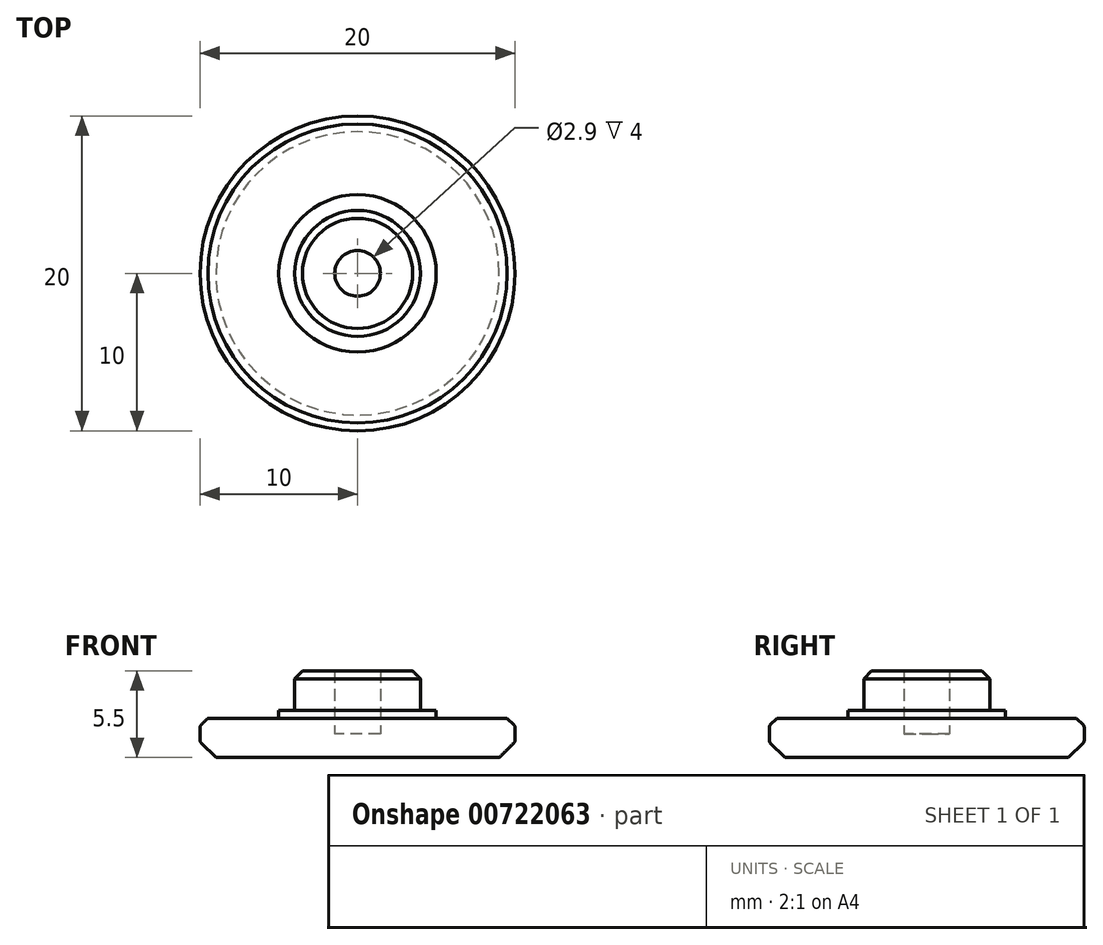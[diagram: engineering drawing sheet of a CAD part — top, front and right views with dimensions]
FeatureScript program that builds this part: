
annotation { "Feature Type Name" : "Feature", "Feature Type Description" : "" }
export const myFeature = defineFeature(function(context is Context, id is Id, definition is map)
    precondition{}
    {
        {
            var Q0;
            Q0=qCreatedBy(makeId("Top.planeOp"),FACE);
            var sketch = newSketch(context, id + "F0", { "sketchPlane" : qUnion([Q0])});
            skCircle(sketch, "E0", {"center": v(0, 0) * mm, "radius": 4 * mm});
            skSolve(sketch);
        }
        {
            var Q0;
            Q0=makeQuery(id+"F0.imprint","IMPRINT",FACE,{"disambiguationData":[TD([[makeQuery(id+"F0.imprint","IMPRINT",EDGE,{"derivedFrom":sQuery(id+"F0.wireOp",EDGE,"E0")}),1.0]])]});
            extrude(context, id + "F1", {"entities" : qUnion([Q0]), "depth" : 5.5 * mm, "offsetDistance" : 25 * mm});
        }
        {
            var Q0;
            Q0=qCreatedBy(makeId("Top.planeOp"),FACE);
            var sketch = newSketch(context, id + "F2", { "sketchPlane" : qUnion([Q0])});
            skCircle(sketch, "E1", {"center": v(0, 0) * mm, "radius": 5 * mm});
            skSolve(sketch);
        }
        {
            var Q0;
            Q0=makeQuery(id+"F2.imprint","IMPRINT",FACE,{"disambiguationData":[TD([[makeQuery(id+"F2.imprint","IMPRINT",EDGE,{"derivedFrom":sQuery(id+"F2.wireOp",EDGE,"E1")}),1.0]])]});
            extrude(context, id + "F3", {"entities" : qUnion([Q0]), "operationType" : NewBodyOperationType.ADD, "depth" : 3 * mm, "offsetDistance" : 25 * mm});
        }
        {
            var Q0;
            Q0=qCreatedBy(makeId("Top.planeOp"),FACE);
            var sketch = newSketch(context, id + "F4", { "sketchPlane" : qUnion([Q0])});
            skCircle(sketch, "E2", {"center": v(0, 0) * mm, "radius": 10 * mm});
            skSolve(sketch);
        }
        {
            var Q0;
            Q0=qSketchRegion(id+"F4",true);
            extrude(context, id + "F5", {"entities" : qUnion([Q0]), "operationType" : NewBodyOperationType.ADD, "depth" : 2.5 * mm, "offsetDistance" : 25 * mm});
        }
        {
            var Q0;
            Q0=makeQuery(id+"F5.opExtrude","CAP_EDGE",EDGE,{"disambiguationData":[OSD([sQuery(id+"F4.wireOp",EDGE,"E2")])],"isStart":true});
            chamfer(context, id + "F6", {"entities" : qUnion([Q0]), "width" : 1 * mm, "tangentPropagation" : true});
        }
        {
            var Q0;
            Q0=makeQuery(id+"F5.opExtrude","CAP_EDGE",EDGE,{"disambiguationData":[OSD([sQuery(id+"F4.wireOp",EDGE,"E2")])],"isStart":false});
            chamfer(context, id + "F7", {"entities" : qUnion([Q0]), "width" : .5 * mm, "tangentPropagation" : true});
        }
        {
            var Q0;
            {var subQ0=sQuery(id+"F4.wireOp",EDGE,"E2");Q0=makeQuery(id+"F6.opChamfer","BLEND_EDGE",EDGE,{"blendedFrom":[makeQuery(id+"F5.opExtrude","CAP_EDGE",EDGE,{"disambiguationData":[OSD([subQ0])],"isStart":true}),makeQuery(id+"F5.opExtrude","SWEPT_FACE",FACE,{"disambiguationData":[OSD([subQ0])]})],"blendedInto":[makeQuery(id+"F5.opExtrude","SWEPT_FACE",FACE,{"disambiguationData":[OSD([subQ0])]})]});}
            var Q1;
            {var subQ0=sQuery(id+"F4.wireOp",EDGE,"E2");Q1=makeQuery(id+"F7.opChamfer","BLEND_EDGE",EDGE,{"blendedFrom":[makeQuery(id+"F5.opExtrude","CAP_EDGE",EDGE,{"disambiguationData":[OSD([subQ0])],"isStart":false}),makeQuery(id+"F5.opExtrude","SWEPT_FACE",FACE,{"disambiguationData":[OSD([subQ0])]})],"blendedInto":[makeQuery(id+"F5.opExtrude","SWEPT_FACE",FACE,{"disambiguationData":[OSD([subQ0])]})]});}
            fillet(context, id + "F8", {"entities" : qUnion([Q0, Q1]), "radius" : .2 * mm, "tangentPropagation" : true, "allowEdgeOverflow" : false});
        }
        {
            var Q0;
            Q0=makeQuery(id+"F1.opExtrude","CAP_EDGE",EDGE,{"disambiguationData":[OSD([sQuery(id+"F0.wireOp",EDGE,"E0")])],"isStart":false});
            chamfer(context, id + "F9", {"entities" : qUnion([Q0]), "width" : .5 * mm, "tangentPropagation" : true});
        }
        {
            var Q0;
            Q0=makeQuery(id+"F1.opExtrude","SWEPT_BODY",BODY,{"disambiguationData":[OSD([sQuery(id+"F0.wireOp",EDGE,"E0")])]});
            transform(context, id + "F10", {"entities" : qUnion([Q0]), "transformType" : TransformType.TRANSLATION_3D, "dx" : -25 * mm, "dy" : 0 * mm, "dz" : 0 * mm, "makeCopy" : true});
        }
        {
            var Q0;
            Q0=qCreatedBy(makeId("Top.planeOp"),FACE);
            var sketch = newSketch(context, id + "F11", { "sketchPlane" : qUnion([Q0])});
            skCircle(sketch, "E3", {"center": v(0, 0) * mm, "radius": 1.45 * mm});
            skSolve(sketch);
        }
        {
            var Q0;
            Q0=makeQuery(id+"F11.imprint","IMPRINT",FACE,{"disambiguationData":[TD([[makeQuery(id+"F11.imprint","IMPRINT",EDGE,{"derivedFrom":sQuery(id+"F11.wireOp",EDGE,"E3")}),1.0]])]});
            var Q1;
            Q1=sQuery(id+"F11.wireOp",EDGE,"E3");
            extrude(context, id + "F12", {"entities" : qUnion([Q0]), "operationType" : NewBodyOperationType.REMOVE, "surfaceEntities" : qUnion([Q1]), "depth" : 11.6 * mm, "offsetDistance" : 25 * mm, "hasSecondDirection" : true, "secondDirectionOppositeDirection" : false, "secondDirectionDepth" : 1.5 * mm});
        }
        {
            var Q0;
            Q0=makeQuery(id+"F10.opPattern","COPY",BODY,{"derivedFrom":makeQuery(id+"F1.opExtrude","SWEPT_BODY",BODY,{"disambiguationData":[OSD([sQuery(id+"F0.wireOp",EDGE,"E0")])]}),"instanceName":"1"});
            deleteBodies(context, id + "F13", {"entities" : qUnion([Q0])});
        }
        {
            var Q0;
            Q0=makeQuery(id+"F1.opExtrude","SWEPT_BODY",BODY,{"disambiguationData":[OSD([sQuery(id+"F0.wireOp",EDGE,"E0")])]});
            transform(context, id + "F14", {"entities" : qUnion([Q0]), "transformType" : TransformType.TRANSLATION_3D, "dx" : -23.4 * mm, "dy" : 0 * mm, "dz" : 0 * mm, "makeCopy" : true});
        }
        {
            var Q0;
            Q0=makeQuery(id+"F14.opPattern","COPY",BODY,{"derivedFrom":makeQuery(id+"F1.opExtrude","SWEPT_BODY",BODY,{"disambiguationData":[OSD([sQuery(id+"F0.wireOp",EDGE,"E0")])]}),"instanceName":"1"});
            deleteBodies(context, id + "F15", {"entities" : qUnion([Q0])});
        }
    });
